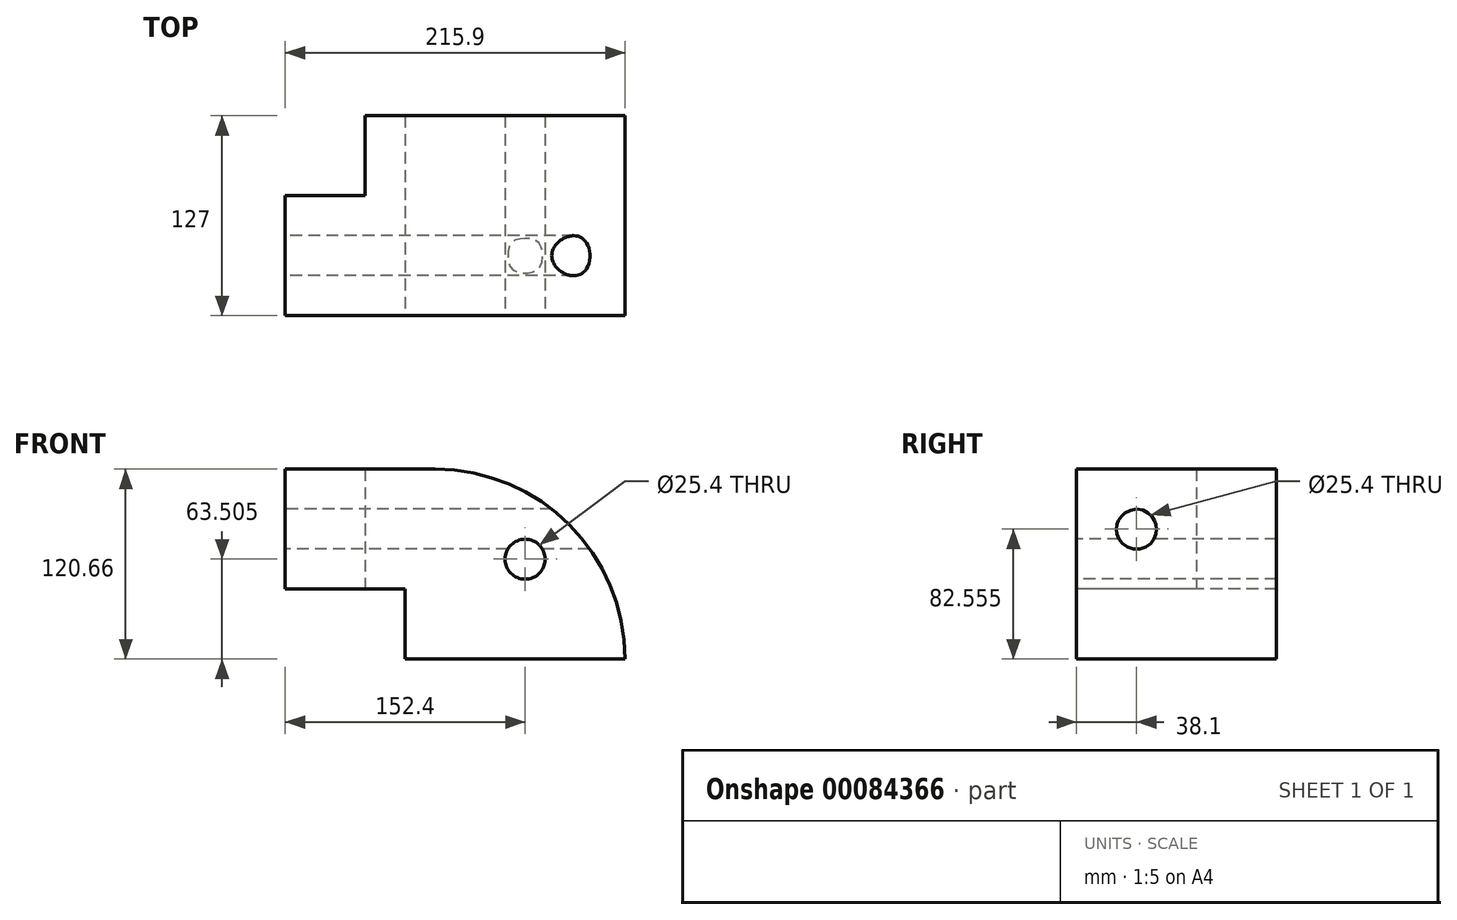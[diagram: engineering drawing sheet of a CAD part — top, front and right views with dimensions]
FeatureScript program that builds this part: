
annotation { "Feature Type Name" : "Feature", "Feature Type Description" : "" }
export const myFeature = defineFeature(function(context is Context, id is Id, definition is map)
    precondition{}
    {
        {
            var Q0;
            Q0=qCreatedBy(makeId("Right.planeOp"),FACE);
            var sketch = newSketch(context, id + "F0", { "sketchPlane" : qUnion([Q0])});
            skLineSegment(sketch, "E0.bottom", {"start": v(-63.5, 60.33) * mm, "end": v(63.5, 60.33) * mm});
            skLineSegment(sketch, "E0.top", {"start": v(-63.5, -60.33) * mm, "end": v(63.5, -60.33) * mm});
            skLineSegment(sketch, "E0.left", {"start": v(-63.5, 60.33) * mm, "end": v(-63.5, -60.33) * mm});
            skLineSegment(sketch, "E0.right", {"start": v(63.5, 60.32) * mm, "end": v(63.5, -60.33) * mm});
            skPoint(sketch, "E0.middle", {"position": v(0, 0) * mm});
            skSolve(sketch);
        }
        {
            var Q0;
            Q0=makeQuery(id+"F0.imprint","IMPRINT",FACE,{"disambiguationData":[TD([[makeQuery(id+"F0.imprint","IMPRINT",EDGE,{"derivedFrom":sQuery(id+"F0.wireOp",EDGE,"E0.bottom")}),-1.0]])]});
            extrude(context, id + "F1", {"entities" : qUnion([Q0]), "depth" : 215.9 * mm});
        }
        {
            var Q0;
            Q0=makeQuery(id+"F1.opExtrude","SWEPT_FACE",FACE,{"disambiguationData":[OSD([sQuery(id+"F0.wireOp",EDGE,"E0.left")])]});
            var sketch = newSketch(context, id + "F2", { "sketchPlane" : qUnion([Q0])});
            skLineSegment(sketch, "E1.bottom", {"start": v(0, -60.33) * mm, "end": v(76.2, -60.33) * mm});
            skLineSegment(sketch, "E1.top", {"start": v(0, -15.88) * mm, "end": v(76.2, -15.88) * mm});
            skLineSegment(sketch, "E1.left", {"start": v(0, -60.33) * mm, "end": v(0, -15.88) * mm});
            skLineSegment(sketch, "E1.right", {"start": v(76.2, -60.33) * mm, "end": v(76.2, -15.88) * mm});
            skSolve(sketch);
        }
        {
            var Q0;
            Q0=makeQuery(id+"F2.imprint","IMPRINT",FACE,{"disambiguationData":[TD([[makeQuery(id+"F2.imprint","IMPRINT",EDGE,{"derivedFrom":sQuery(id+"F2.wireOp",EDGE,"E1.bottom")}),-1.0]])]});
            extrude(context, id + "F3", {"entities" : qUnion([Q0]), "operationType" : NewBodyOperationType.REMOVE, "oppositeDirection" : true, "depth" : 127 * mm});
        }
        {
            var Q0;
            Q0=makeQuery(id+"F1.opExtrude","CAP_FACE",FACE,{"disambiguationData":[OSD([sQuery(id+"F0.wireOp",EDGE,"E0.bottom"),sQuery(id+"F0.wireOp",EDGE,"E0.top"),sQuery(id+"F0.wireOp",EDGE,"E0.left"),sQuery(id+"F0.wireOp",EDGE,"E0.right")])],"isStart":true});
            var sketch = newSketch(context, id + "F4", { "sketchPlane" : qUnion([Q0])});
            skLineSegment(sketch, "E2.bottom", {"start": v(-63.5, 60.32) * mm, "end": v(-12.7, 60.32) * mm});
            skLineSegment(sketch, "E2.top", {"start": v(-63.5, -15.88) * mm, "end": v(-12.7, -15.88) * mm});
            skLineSegment(sketch, "E2.left", {"start": v(-63.5, 60.32) * mm, "end": v(-63.5, -15.88) * mm});
            skLineSegment(sketch, "E2.right", {"start": v(-12.7, 60.32) * mm, "end": v(-12.7, -15.88) * mm});
            skLineSegment(sketch, "E3.bottom", {"start": v(-63.5, -15.88) * mm, "end": v(63.5, -15.88) * mm});
            skLineSegment(sketch, "E3.top", {"start": v(-63.5, -15.88) * mm, "end": v(63.5, -15.88) * mm});
            skLineSegment(sketch, "E3.left", {"start": v(-63.5, -15.88) * mm, "end": v(-63.5, -15.88) * mm});
            skLineSegment(sketch, "E3.right", {"start": v(63.5, -15.88) * mm, "end": v(63.5, -15.87) * mm});
            skSolve(sketch);
        }
        {
            var Q0;
            Q0=makeQuery(id+"F4.imprint","IMPRINT",FACE,{"disambiguationData":[TD([[makeQuery(id+"F4.imprint","IMPRINT",EDGE,{"derivedFrom":sQuery(id+"F4.wireOp",EDGE,"E2.bottom")}),1.0]])]});
            extrude(context, id + "F5", {"entities" : qUnion([Q0]), "operationType" : NewBodyOperationType.REMOVE, "oppositeDirection" : true, "depth" : 50.8 * mm});
        }
        {
            var Q0;
            Q0=makeQuery(id+"F1.opExtrude","CAP_FACE",FACE,{"disambiguationData":[OSD([sQuery(id+"F0.wireOp",EDGE,"E0.bottom"),sQuery(id+"F0.wireOp",EDGE,"E0.top"),sQuery(id+"F0.wireOp",EDGE,"E0.left"),sQuery(id+"F0.wireOp",EDGE,"E0.right")])],"isStart":true});
            var sketch = newSketch(context, id + "F6", { "sketchPlane" : qUnion([Q0])});
            skCircle(sketch, "E4", {"center": v(25.4, 22.22) * mm, "radius": 12.7 * mm});
            skSolve(sketch);
        }
        {
            var Q0;
            Q0=makeQuery(id+"F1.opExtrude","SWEPT_FACE",FACE,{"disambiguationData":[OSD([sQuery(id+"F0.wireOp",EDGE,"E0.left")])]});
            var sketch = newSketch(context, id + "F7", { "sketchPlane" : qUnion([Q0])});
            skLineSegment(sketch, "E5.bottom", {"start": v(215.9, -60.33) * mm, "end": v(141.2, -60.33) * mm});
            skLineSegment(sketch, "E5.left", {"start": v(215.9, -60.33) * mm, "end": v(215.9, -8.03) * mm});
            skPoint(sketch, "E6", {"position": v(152.4, 3.17) * mm});
            skSolve(sketch);
        }
        {
            var Q0;
            Q0=sQuery(id+"F7.wireOp",VERTEX,"E6");
            var Q1;
            Q1=makeQuery(id+"F1.opExtrude","SWEPT_BODY",BODY,{"disambiguationData":[OSD([sQuery(id+"F0.wireOp",EDGE,"E0.bottom"),sQuery(id+"F0.wireOp",EDGE,"E0.top"),sQuery(id+"F0.wireOp",EDGE,"E0.left"),sQuery(id+"F0.wireOp",EDGE,"E0.right")])]});
            hole(context, id + "F8", {"style" : HoleStyle.SIMPLE, "endStyle" : HoleEndStyle.BLIND, "holeDiameter" : 25.4 * mm, "holeDepth" : 127 * mm, "locations" : qUnion([Q0]), "scope" : qUnion([Q1])});
        }
        {
            var Q0;
            Q0=makeQuery(id+"F1.opExtrude","CAP_EDGE",EDGE,{"disambiguationData":[OSD([sQuery(id+"F0.wireOp",EDGE,"E0.bottom")])],"isStart":false});
            fillet(context, id + "F9", {"entities" : qUnion([Q0]), "radius" : 120.65 * mm, "tangentPropagation" : true, "allowEdgeOverflow" : false});
        }
        {
            var Q0;
            Q0=sQuery(id+"F6.wireOp",VERTEX,"E4.center");
            var Q1;
            Q1=makeQuery(id+"F1.opExtrude","SWEPT_BODY",BODY,{"disambiguationData":[OSD([sQuery(id+"F0.wireOp",EDGE,"E0.bottom"),sQuery(id+"F0.wireOp",EDGE,"E0.top"),sQuery(id+"F0.wireOp",EDGE,"E0.left"),sQuery(id+"F0.wireOp",EDGE,"E0.right")])]});
            hole(context, id + "F10", {"style" : HoleStyle.SIMPLE, "endStyle" : HoleEndStyle.THROUGH, "holeDiameter" : 25.4 * mm, "locations" : qUnion([Q0]), "scope" : qUnion([Q1]), "isTappedThrough" : true});
        }
    });
